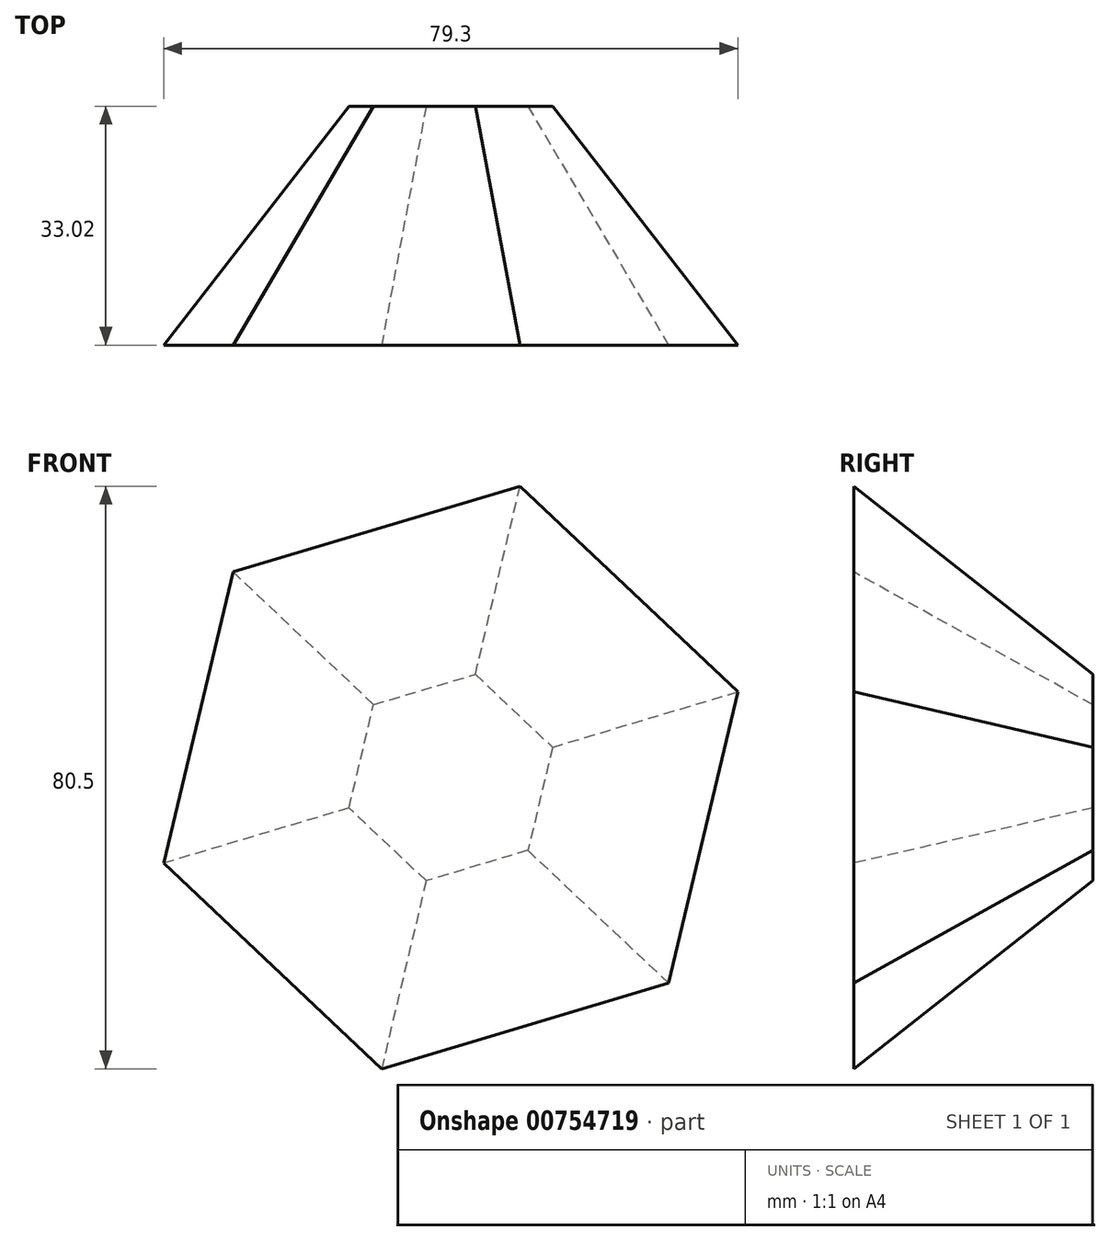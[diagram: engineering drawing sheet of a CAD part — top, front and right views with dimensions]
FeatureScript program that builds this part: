
annotation { "Feature Type Name" : "Feature", "Feature Type Description" : "" }
export const myFeature = defineFeature(function(context is Context, id is Id, definition is map)
    precondition{}
    {
        {
            var Q0;
            Q0=qCreatedBy(makeId("Front.planeOp"),FACE);
            var sketch = newSketch(context, id + "F0", { "sketchPlane" : qUnion([Q0])});
            skCircle(sketch, "E0.cCircle", {"center": v(0, 0) * mm, "radius": 35.83 * mm, "construction": true});
            skLineSegment(sketch, "E0.0", {"start": v(9.57, 40.25) * mm, "end": v(39.65, 11.84) * mm});
            skLineSegment(sketch, "E0.1", {"start": v(39.65, 11.84) * mm, "end": v(30.08, -28.41) * mm});
            skLineSegment(sketch, "E0.2", {"start": v(30.08, -28.41) * mm, "end": v(-9.57, -40.25) * mm});
            skLineSegment(sketch, "E0.3", {"start": v(-9.57, -40.25) * mm, "end": v(-39.65, -11.84) * mm});
            skLineSegment(sketch, "E0.4", {"start": v(-39.65, -11.84) * mm, "end": v(-30.08, 28.41) * mm});
            skLineSegment(sketch, "E0.5", {"start": v(-30.08, 28.41) * mm, "end": v(9.57, 40.25) * mm});
            skPoint(sketch, "E0.0.midPoint", {"position": v(24.6, 26.05) * mm});
            skSolve(sketch);
        }
        {
            var Q0;
            Q0=makeQuery(id+"F0.imprint","IMPRINT",FACE,{"disambiguationData":[TD([[makeQuery(id+"F0.imprint","IMPRINT",EDGE,{"derivedFrom":sQuery(id+"F0.wireOp",EDGE,"E0.0")}),-1.0]])]});
            cPlane(context, id + "F1", {"entities" : qUnion([Q0]), "cplaneType" : CPlaneType.OFFSET, "offset" : 33.02 * mm, "oppositeDirection" : true, "width" : 152.4 * mm, "height" : 152.4 * mm});
        }
        {
            var Q0;
            Q0=qCreatedBy(id+"F1.planeOp",FACE);
            var sketch = newSketch(context, id + "F2", { "sketchPlane" : qUnion([Q0])});
            skCircle(sketch, "E1.cCircle", {"center": v(0, 0) * mm, "radius": 12.7 * mm, "construction": true});
            skLineSegment(sketch, "E1.0", {"start": v(3.4, 14.27) * mm, "end": v(14.05, 4.2) * mm});
            skLineSegment(sketch, "E1.1", {"start": v(14.05, 4.2) * mm, "end": v(10.66, -10.07) * mm});
            skLineSegment(sketch, "E1.2", {"start": v(10.66, -10.07) * mm, "end": v(-3.4, -14.27) * mm});
            skLineSegment(sketch, "E1.3", {"start": v(-3.4, -14.27) * mm, "end": v(-14.05, -4.2) * mm});
            skLineSegment(sketch, "E1.4", {"start": v(-14.05, -4.2) * mm, "end": v(-10.66, 10.07) * mm});
            skLineSegment(sketch, "E1.5", {"start": v(-10.66, 10.07) * mm, "end": v(3.4, 14.27) * mm});
            skPoint(sketch, "E1.0.midPoint", {"position": v(8.72, 9.23) * mm});
            skSolve(sketch);
        }
        {
            var Q0;
            Q0=makeQuery(id+"F2.imprint","IMPRINT",FACE,{"disambiguationData":[TD([[makeQuery(id+"F2.imprint","IMPRINT",EDGE,{"derivedFrom":sQuery(id+"F2.wireOp",EDGE,"E1.0")}),-1.0]])]});
            var Q1;
            Q1=makeQuery(id+"F0.imprint","IMPRINT",FACE,{"disambiguationData":[TD([[makeQuery(id+"F0.imprint","IMPRINT",EDGE,{"derivedFrom":sQuery(id+"F0.wireOp",EDGE,"E0.0")}),-1.0]])]});
            loft(context, id + "F3", {"sheetProfilesArray" : [{ "sheetProfileEntities" : qUnion([Q0]) }, { "sheetProfileEntities" : qUnion([Q1]) }]});
        }
    });
